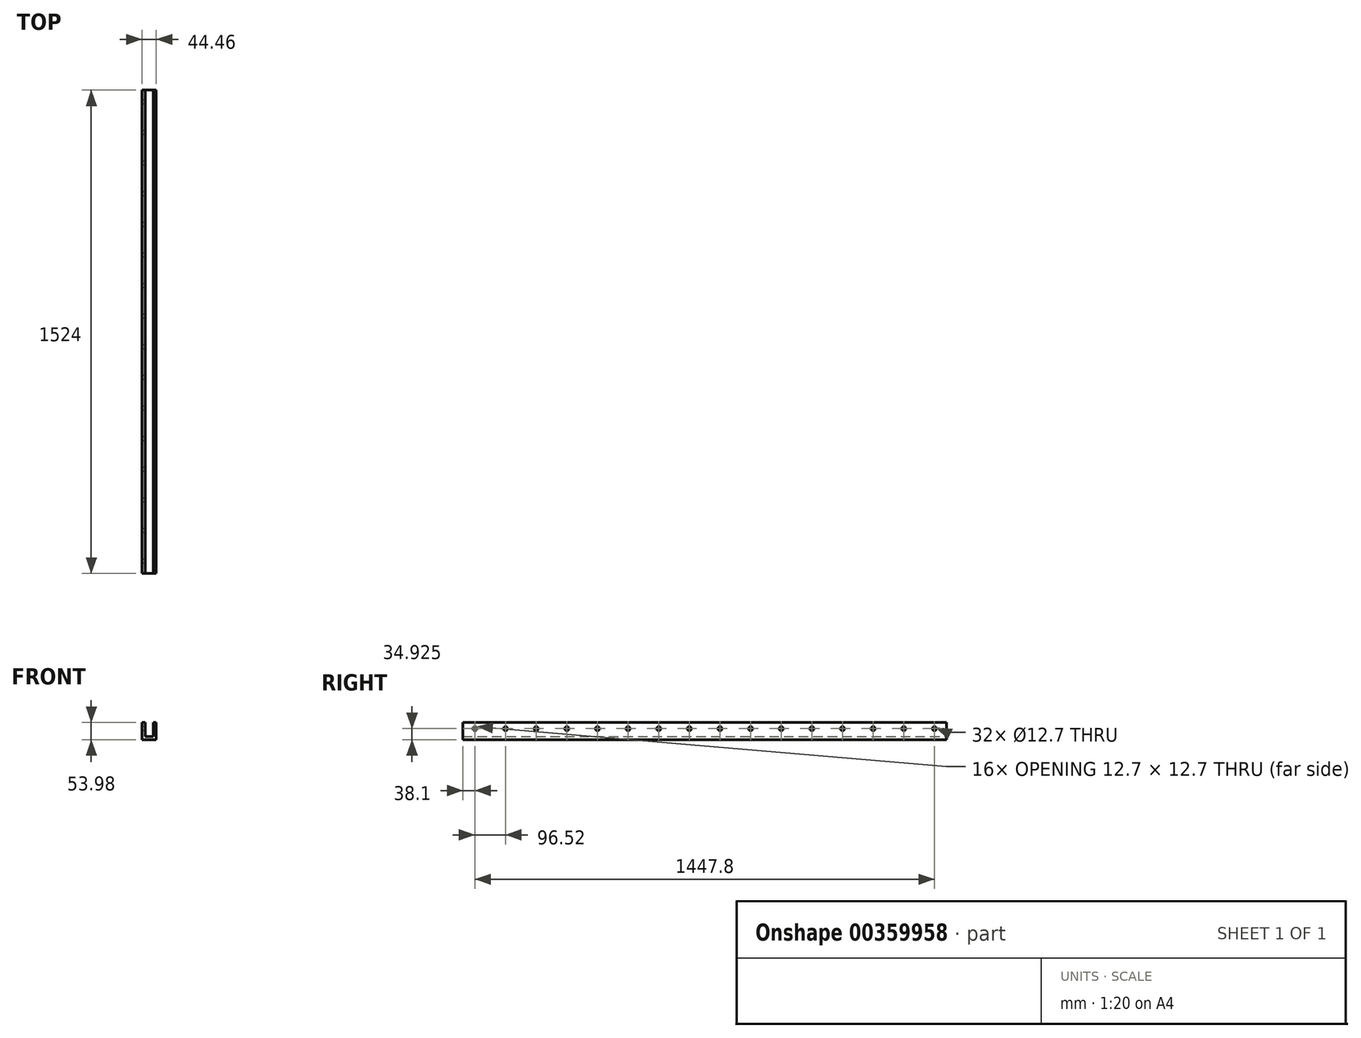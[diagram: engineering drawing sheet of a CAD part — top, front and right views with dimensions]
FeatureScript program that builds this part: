
annotation { "Feature Type Name" : "Feature", "Feature Type Description" : "" }
export const myFeature = defineFeature(function(context is Context, id is Id, definition is map)
    precondition{}
    {
        {
            var Q0;
            Q0=qCreatedBy(makeId("Front.planeOp"),FACE);
            var sketch = newSketch(context, id + "F0", { "sketchPlane" : qUnion([Q0])});
            skLineSegment(sketch, "E0", {"start": v(0, 0) * mm, "end": v(22.22, 0) * mm});
            skLineSegment(sketch, "E1", {"start": v(22.22, 0) * mm, "end": v(22.22, 53.98) * mm});
            skLineSegment(sketch, "E2", {"start": v(22.23, 53.98) * mm, "end": v(12.7, 53.98) * mm});
            skLineSegment(sketch, "E3", {"start": v(12.7, 53.98) * mm, "end": v(12.7, 9.53) * mm});
            skLineSegment(sketch, "E4", {"start": v(12.7, 9.53) * mm, "end": v(-12.7, 9.53) * mm});
            skLineSegment(sketch, "E5", {"start": v(-12.7, 9.53) * mm, "end": v(-12.7, 53.98) * mm});
            skLineSegment(sketch, "E6", {"start": v(-12.7, 53.98) * mm, "end": v(-22.23, 53.98) * mm});
            skLineSegment(sketch, "E7", {"start": v(-22.23, 53.98) * mm, "end": v(-22.22, 0) * mm});
            skLineSegment(sketch, "E8", {"start": v(-22.22, 0) * mm, "end": v(0, 0) * mm});
            skSolve(sketch);
        }
        {
            var Q0;
            Q0 = qSketchRegion(id + "F0", true);
            extrude(context, id + "F1", {"entities" : qUnion([Q0]), "depth" : 1524 * mm});
        }
        {
            var Q0;
            Q0=qCreatedBy(makeId("Right.planeOp"),FACE);
            var sketch = newSketch(context, id + "F2", { "sketchPlane" : qUnion([Q0])});
            skLineSegment(sketch, "E9", {"start": v(-38.1, 9.53) * mm, "end": v(-38.1, 0) * mm, "construction": true});
            skPoint(sketch, "E10", {"position": v(-38.1, 34.93) * mm});
            skCircle(sketch, "E11", {"center": v(-38.1, 34.93) * mm, "radius": 24.13 * mm, "construction": true});
            skLineSegment(sketch, "E12", {"start": v(-38.1, 9.53) * mm, "end": v(-38.1, 34.93) * mm, "construction": true});
            skCircle(sketch, "E13", {"center": v(-38.1, 34.93) * mm, "radius": 6.35 * mm});
            skCircle(sketch, "E14.1.0.0", {"center": v(-134.62, 34.92) * mm, "radius": 6.35 * mm});
            skCircle(sketch, "E14.2.0.0", {"center": v(-231.14, 34.92) * mm, "radius": 6.35 * mm});
            skCircle(sketch, "E14.3.0.0", {"center": v(-327.66, 34.92) * mm, "radius": 6.35 * mm});
            skCircle(sketch, "E14.4.0.0", {"center": v(-424.18, 34.92) * mm, "radius": 6.35 * mm});
            skCircle(sketch, "E14.5.0.0", {"center": v(-520.7, 34.92) * mm, "radius": 6.35 * mm});
            skCircle(sketch, "E14.6.0.0", {"center": v(-617.22, 34.92) * mm, "radius": 6.35 * mm});
            skCircle(sketch, "E14.7.0.0", {"center": v(-713.74, 34.92) * mm, "radius": 6.35 * mm});
            skCircle(sketch, "E14.8.0.0", {"center": v(-810.26, 34.92) * mm, "radius": 6.35 * mm});
            skCircle(sketch, "E14.9.0.0", {"center": v(-906.78, 34.92) * mm, "radius": 6.35 * mm});
            skCircle(sketch, "E14.10.0.0", {"center": v(-1003.3, 34.92) * mm, "radius": 6.35 * mm});
            skCircle(sketch, "E14.11.0.0", {"center": v(-1099.82, 34.92) * mm, "radius": 6.35 * mm});
            skCircle(sketch, "E14.12.0.0", {"center": v(-1196.34, 34.92) * mm, "radius": 6.35 * mm});
            skCircle(sketch, "E14.13.0.0", {"center": v(-1292.86, 34.92) * mm, "radius": 6.35 * mm});
            skCircle(sketch, "E14.14.0.0", {"center": v(-1389.38, 34.92) * mm, "radius": 6.35 * mm});
            skCircle(sketch, "E14.15.0.0", {"center": v(-1485.9, 34.92) * mm, "radius": 6.35 * mm});
            skLineSegment(sketch, "E14.direction1", {"start": v(-38.1, 34.93) * mm, "end": v(-134.62, 34.93) * mm, "construction": true});
            skSolve(sketch);
        }
        {
            var Q0;
            Q0 = qSketchRegion(id + "F2", true);
            extrude(context, id + "F3", {"entities" : qUnion([Q0]), "operationType" : NewBodyOperationType.REMOVE, "endBound" : BoundingType.THROUGH_ALL, "depth" : 25.4 * mm, "hasSecondDirection" : true, "secondDirectionBound" : SecondDirectionBoundingType.THROUGH_ALL, "secondDirectionOppositeDirection" : true, "secondDirectionDepth" : 25.4 * mm});
        }
    });
